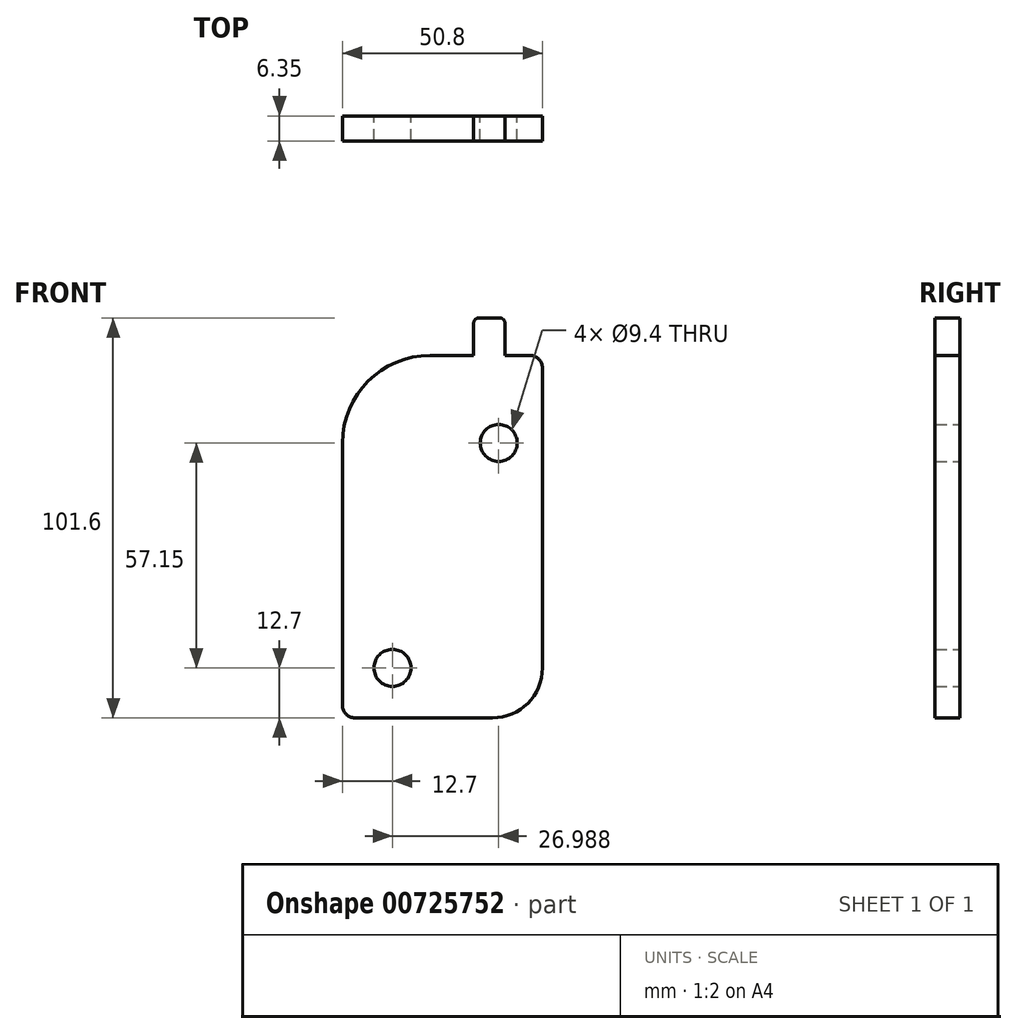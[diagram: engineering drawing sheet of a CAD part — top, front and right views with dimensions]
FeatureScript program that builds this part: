
annotation { "Feature Type Name" : "Feature", "Feature Type Description" : "" }
export const myFeature = defineFeature(function(context is Context, id is Id, definition is map)
    precondition{}
    {
        {
            var Q0;
            Q0=qCreatedBy(makeId("Front.planeOp"),FACE);
            var sketch = newSketch(context, id + "F0", { "sketchPlane" : qUnion([Q0])});
            skLineSegment(sketch, "E0.bottom", {"start": v(0, 12.7) * mm, "end": v(0, 88.9) * mm});
            skLineSegment(sketch, "E0.top", {"start": v(-50.8, 3.17) * mm, "end": v(-50.8, 69.85) * mm});
            skLineSegment(sketch, "E0.left", {"start": v(-12.7, 0) * mm, "end": v(-47.62, 0) * mm});
            skLineSegment(sketch, "E0.right", {"start": v(-3.17, 92.08) * mm, "end": v(-9.52, 92.08) * mm});
            skLineSegment(sketch, "E1.bottom", {"start": v(-9.52, 92.08) * mm, "end": v(-9.52, 100.33) * mm});
            skLineSegment(sketch, "E1.top", {"start": v(-17.46, 92.08) * mm, "end": v(-17.46, 100.33) * mm});
            skLineSegment(sketch, "E1.right", {"start": v(-10.8, 101.6) * mm, "end": v(-16.2, 101.6) * mm});
            skPoint(sketch, "E2.visualSharp", {"position": v(-50.8, 92.08) * mm});
            skArc(sketch, "E2.filletArc", {"start": v(-28.58, 92.07) * mm, "mid": v(-44.3, 85.57) * mm, "end": v(-50.8, 69.85) * mm});
            skPoint(sketch, "E3.visualSharp", {"position": v(0, 0) * mm});
            skArc(sketch, "E3.filletArc", {"start": v(-12.7, 0) * mm, "mid": v(-3.72, 3.72) * mm, "end": v(0, 12.7) * mm});
            skPoint(sketch, "E4.visualSharp", {"position": v(-50.8, 0) * mm});
            skArc(sketch, "E4.filletArc", {"start": v(-50.8, 3.17) * mm, "mid": v(-49.87, 0.93) * mm, "end": v(-47.62, 0) * mm});
            skPoint(sketch, "E5.visualSharp", {"position": v(0, 92.08) * mm});
            skArc(sketch, "E5.filletArc", {"start": v(0, 88.9) * mm, "mid": v(-0.93, 91.15) * mm, "end": v(-3.17, 92.08) * mm});
            skLineSegment(sketch, "E6.trimOffspring", {"start": v(-17.46, 92.08) * mm, "end": v(-28.57, 92.08) * mm});
            skPoint(sketch, "E7.visualSharp", {"position": v(-17.46, 101.6) * mm});
            skArc(sketch, "E7.filletArc", {"start": v(-16.2, 101.6) * mm, "mid": v(-17.1, 101.23) * mm, "end": v(-17.46, 100.33) * mm});
            skPoint(sketch, "E8.visualSharp", {"position": v(-9.52, 101.6) * mm});
            skArc(sketch, "E8.filletArc", {"start": v(-9.52, 100.33) * mm, "mid": v(-9.9, 101.23) * mm, "end": v(-10.8, 101.6) * mm});
            skCircle(sketch, "E9", {"center": v(-38.1, 12.7) * mm, "radius": 4.7 * mm});
            skCircle(sketch, "E10", {"center": v(-11.11, 69.85) * mm, "radius": 4.7 * mm});
            skSolve(sketch);
        }
        {
            var Q0;
            Q0 = qSketchRegion(id + "F0", true);
            extrude(context, id + "F1", {"entities" : qUnion([Q0]), "depth" : 6.35 * mm, "offsetDistance" : 25.4 * mm});
        }
    });
